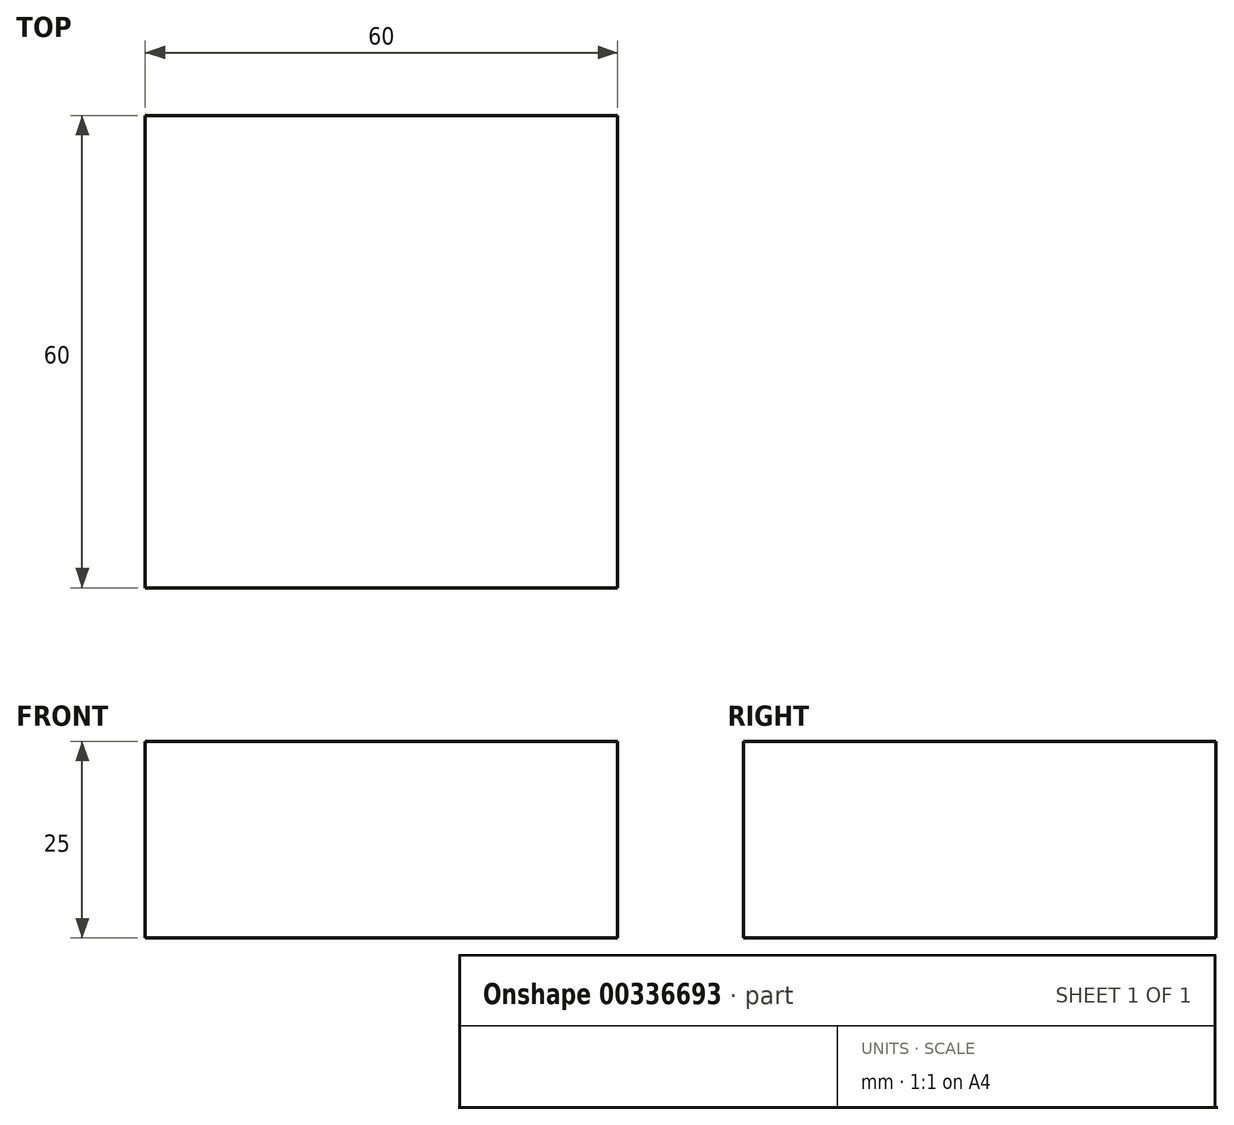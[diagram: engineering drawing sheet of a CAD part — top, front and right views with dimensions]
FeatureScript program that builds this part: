
annotation { "Feature Type Name" : "Feature", "Feature Type Description" : "" }
export const myFeature = defineFeature(function(context is Context, id is Id, definition is map)
    precondition{}
    {
        {
            var Q0;
            Q0=qCreatedBy(makeId("Top.planeOp"),FACE);
            var sketch = newSketch(context, id + "F0", { "sketchPlane" : qUnion([Q0])});
            skLineSegment(sketch, "E0.bottom", {"start": v(0, 0) * mm, "end": v(60, 0) * mm});
            skLineSegment(sketch, "E0.top", {"start": v(0, -60) * mm, "end": v(60, -60) * mm});
            skLineSegment(sketch, "E0.left", {"start": v(0, 0) * mm, "end": v(0, -60) * mm});
            skLineSegment(sketch, "E0.right", {"start": v(60, 0) * mm, "end": v(60, -60) * mm});
            skSolve(sketch);
        }
        {
            var Q0;
            Q0=makeQuery(id+"F0.imprint","IMPRINT",FACE,{"disambiguationData":[TD([[makeQuery(id+"F0.imprint","IMPRINT",EDGE,{"derivedFrom":sQuery(id+"F0.wireOp",EDGE,"E0.bottom")}),-1.0]])]});
            extrude(context, id + "F1", {"entities" : qUnion([Q0]), "depth" : 25 * mm, "offsetDistance" : 25 * mm});
        }
    });
